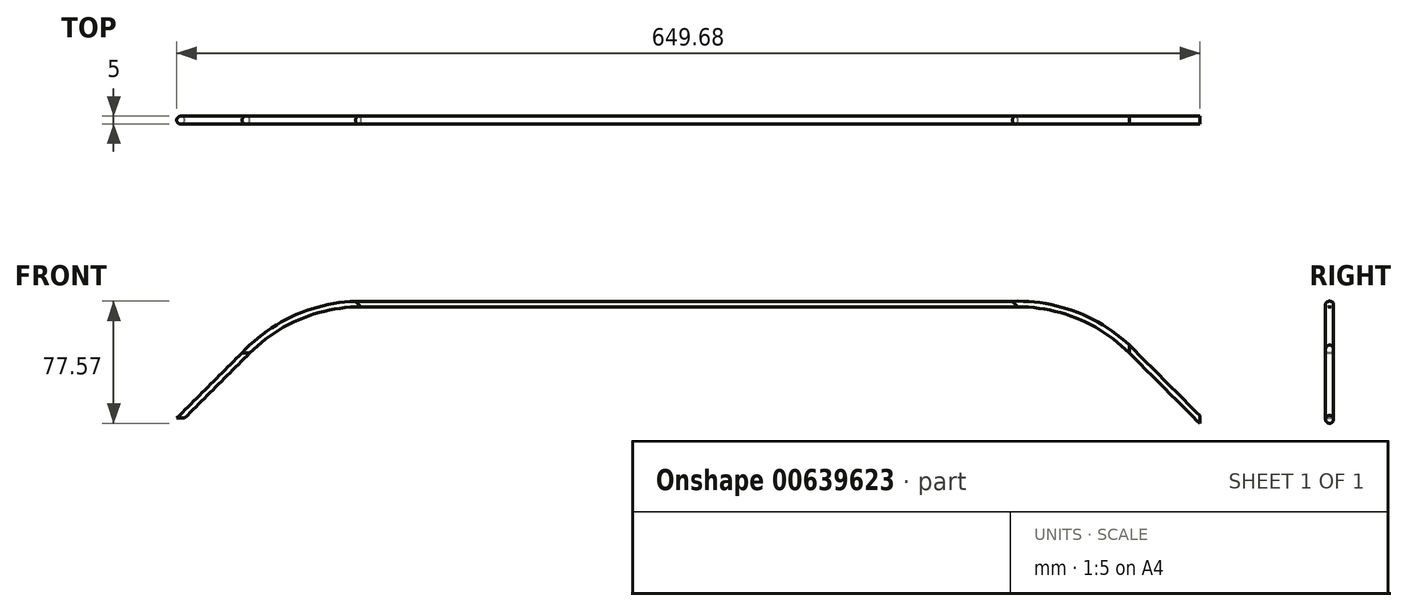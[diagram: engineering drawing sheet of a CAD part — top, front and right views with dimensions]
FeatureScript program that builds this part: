
annotation { "Feature Type Name" : "Feature", "Feature Type Description" : "" }
export const myFeature = defineFeature(function(context is Context, id is Id, definition is map)
    precondition{}
    {
        {
            var Q0;
            Q0=qCreatedBy(makeId("Top.planeOp"),FACE);
            var sketch = newSketch(context, id + "F0", { "sketchPlane" : qUnion([Q0])});
            skPoint(sketch, "E0", {"position": v(0, 0) * mm});
            skLineSegment(sketch, "E1", {"start": v(0, 5.66) * mm, "end": v(0, -4.92) * mm, "construction": true});
            skLineSegment(sketch, "E2", {"start": v(-6.35, 0) * mm, "end": v(5.42, 0) * mm, "construction": true});
            skCircle(sketch, "E3", {"center": v(-2.5, 0) * mm, "radius": 2.5 * mm});
            skSolve(sketch);
        }
        {
            var Q0;
            Q0=qCreatedBy(makeId("Front.planeOp"),FACE);
            var sketch = newSketch(context, id + "F1", { "sketchPlane" : qUnion([Q0])});
            skLineSegment(sketch, "E4", {"start": v(0, 0) * mm, "end": v(41.42, 41.42) * mm});
            skLineSegment(sketch, "E5", {"start": v(112.13, 70.71) * mm, "end": v(529.29, 70.71) * mm});
            skLineSegment(sketch, "E6", {"start": v(600, 41.42) * mm, "end": v(644.68, -3.26) * mm});
            skPoint(sketch, "E7.visualSharp", {"position": v(70.71, 70.71) * mm});
            skArc(sketch, "E7.filletArc", {"start": v(112.13, 70.71) * mm, "mid": v(73.86, 63.1) * mm, "end": v(41.42, 41.42) * mm});
            skPoint(sketch, "E8.visualSharp", {"position": v(570.71, 70.71) * mm});
            skArc(sketch, "E8.filletArc", {"start": v(600, 41.42) * mm, "mid": v(567.56, 63.1) * mm, "end": v(529.29, 70.71) * mm});
            skSolve(sketch);
        }
        {
            var Q0;
            Q0=makeQuery(id+"F0.imprint","IMPRINT",FACE,{"disambiguationData":[TD([[makeQuery(id+"F0.imprint","IMPRINT",EDGE,{"derivedFrom":sQuery(id+"F0.wireOp",EDGE,"E3")}),1.0]])]});
            var Q1;
            Q1=sQuery(id+"F1.wireOp",EDGE,"E4");
            var Q2;
            Q2=sQuery(id+"F1.wireOp",EDGE,"E7.filletArc");
            var Q3;
            Q3=sQuery(id+"F1.wireOp",EDGE,"E5");
            var Q4;
            Q4=sQuery(id+"F1.wireOp",EDGE,"E8.filletArc");
            var Q5;
            Q5=sQuery(id+"F1.wireOp",EDGE,"E6");
            sweep(context, id + "F2", {"profiles" : qUnion([Q0]), "path" : qUnion([Q1, Q2, Q3, Q4, Q5])});
        }
    });
